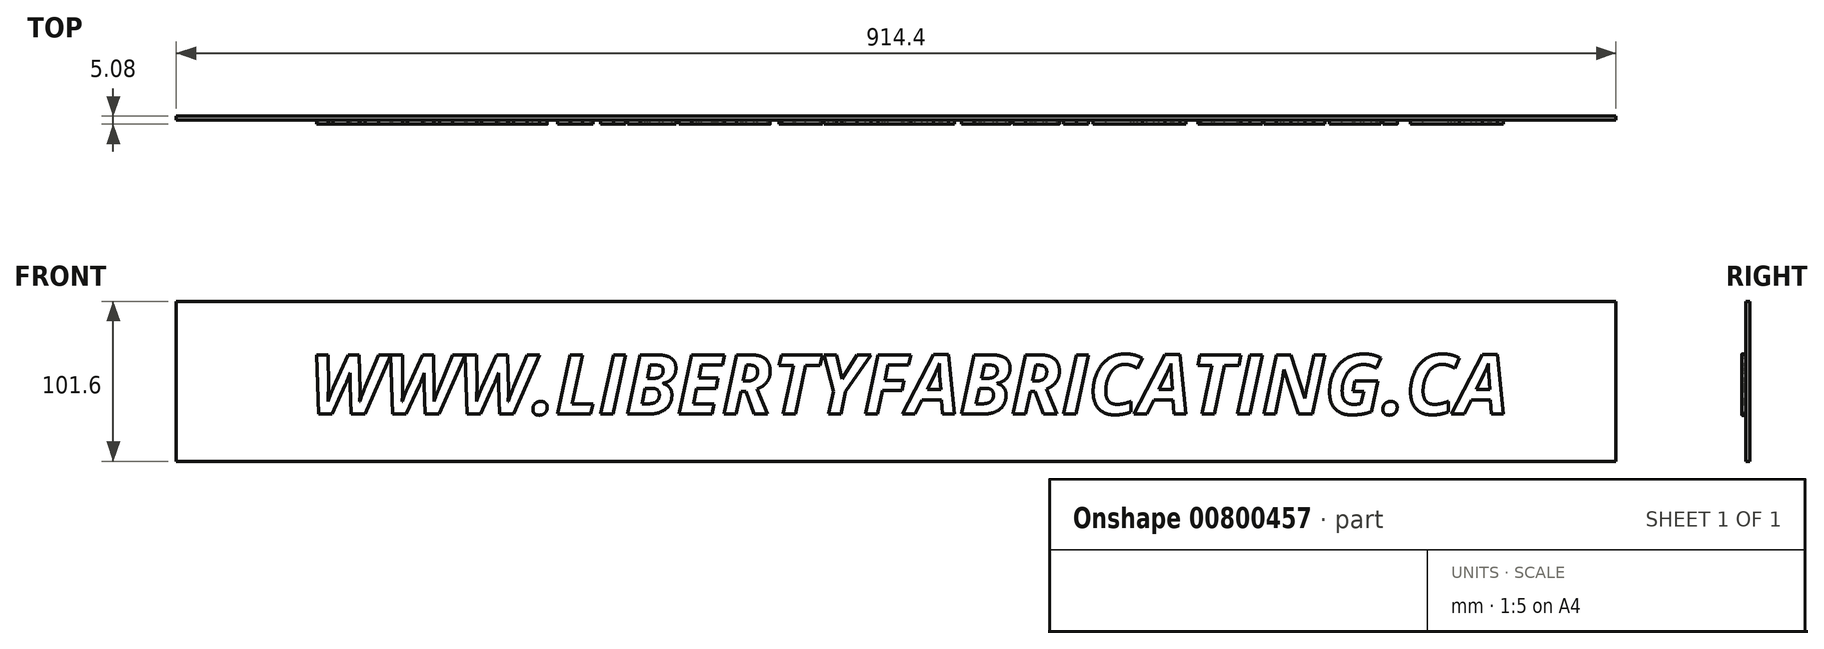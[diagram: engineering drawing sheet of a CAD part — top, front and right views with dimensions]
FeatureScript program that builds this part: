
annotation { "Feature Type Name" : "Feature", "Feature Type Description" : "" }
export const myFeature = defineFeature(function(context is Context, id is Id, definition is map)
    precondition{}
    {
        {
            var Q0;
            Q0=qCreatedBy(makeId("Front.planeOp"),FACE);
            var sketch = newSketch(context, id + "F0", { "sketchPlane" : qUnion([Q0])});
            skLineSegment(sketch, "E0.bottom", {"start": v(-207.56, 16.24) * mm, "end": v(706.84, 16.24) * mm});
            skLineSegment(sketch, "E0.top", {"start": v(-207.56, -85.36) * mm, "end": v(706.84, -85.36) * mm});
            skLineSegment(sketch, "E0.left", {"start": v(-207.56, 16.24) * mm, "end": v(-207.56, -85.36) * mm});
            skLineSegment(sketch, "E0.right", {"start": v(706.84, 16.24) * mm, "end": v(706.84, -85.36) * mm});
            skSolve(sketch);
        }
        {
            var Q0;
            Q0=makeQuery(id+"F0.imprint","IMPRINT",FACE,{"disambiguationData":[TD([[makeQuery(id+"F0.imprint","IMPRINT",EDGE,{"derivedFrom":sQuery(id+"F0.wireOp",EDGE,"E0.bottom")}),-1.0]])]});
            extrude(context, id + "F1", {"entities" : qUnion([Q0]), "depth" : 2.54 * mm, "offsetDistance" : 25.4 * mm});
        }
        {
            var Q0;
            Q0=makeQuery(id+"F1.opExtrude","CAP_FACE",FACE,{"disambiguationData":[OSD([sQuery(id+"F0.wireOp",EDGE,"E0.bottom"),sQuery(id+"F0.wireOp",EDGE,"E0.top"),sQuery(id+"F0.wireOp",EDGE,"E0.left"),sQuery(id+"F0.wireOp",EDGE,"E0.right")])],"isStart":false});
            var sketch = newSketch(context, id + "F2", { "sketchPlane" : qUnion([Q0])});
            skText(sketch, "E1", { "text": "WWW.LIBERTYFABRICATING.CA", "fontName": "OpenSans-BoldItalic.ttf"});
            const initialGuessF2  = {"E1": [-0.1232, -0.0554, 1, 0, 0.03797]};
            skSetInitialGuess(sketch, initialGuessF2);
            skSolve(sketch);
        }
        {
            var Q0;
            Q0 = qSketchRegion(id + "F2", true);
            extrude(context, id + "F3", {"entities" : qUnion([Q0]), "operationType" : NewBodyOperationType.ADD, "depth" : 2.54 * mm, "offsetDistance" : 25.4 * mm});
        }
    });
